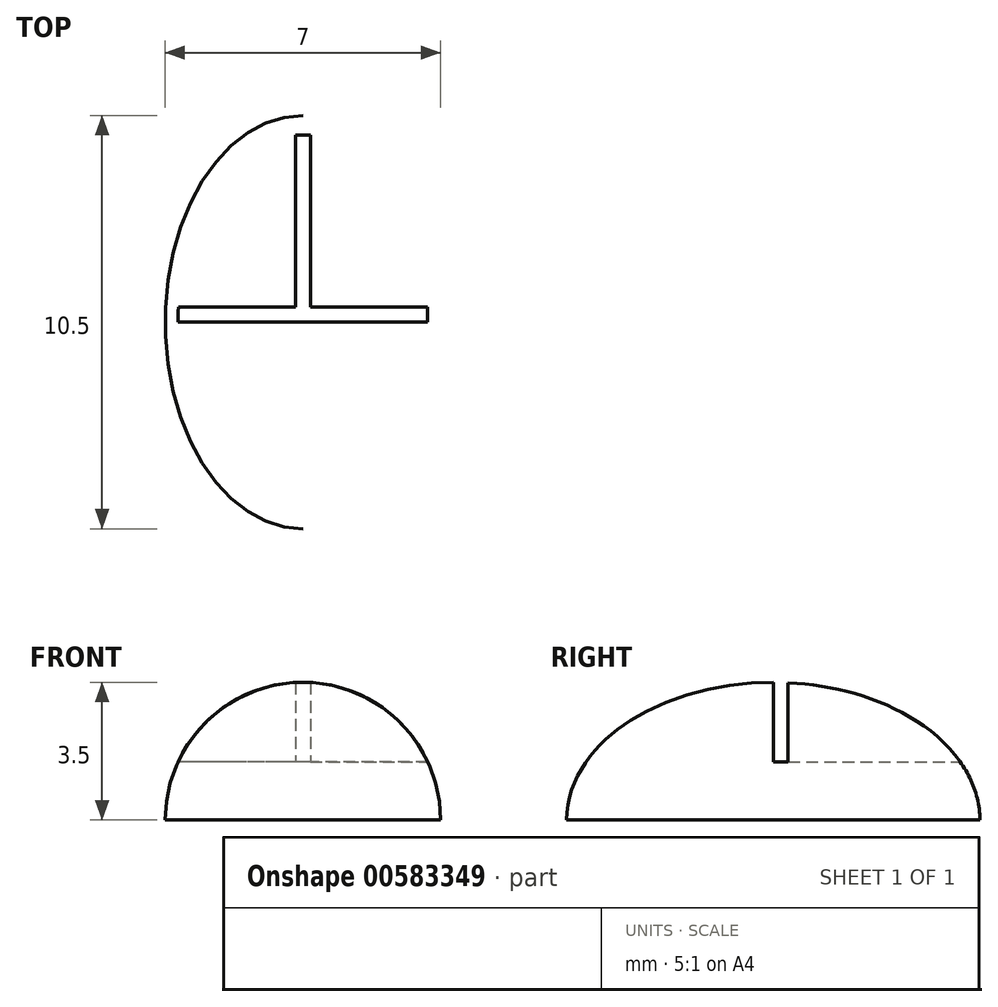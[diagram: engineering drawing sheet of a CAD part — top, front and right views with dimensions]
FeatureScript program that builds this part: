
annotation { "Feature Type Name" : "Feature", "Feature Type Description" : "" }
export const myFeature = defineFeature(function(context is Context, id is Id, definition is map)
    precondition{}
    {
        {
            var Q0;
            Q0=qCreatedBy(makeId("Top.planeOp"),FACE);
            var sketch = newSketch(context, id + "F0", { "sketchPlane" : qUnion([Q0])});
            skEllipticalArc(sketch, "E0", {});
            skLineSegment(sketch, "E1", {"start": v(0, 0) * mm, "end": v(0, 1.86) * mm});
            skPoint(sketch, "E1.endSnap0", {"position": v(0, 5.25) * mm});
            skLineSegment(sketch, "E2", {"start": v(0, 1.86) * mm, "end": v(0, 5.25) * mm});
            skLineSegment(sketch, "E3", {"start": v(0, 0) * mm, "end": v(0, -5.25) * mm});
            const initialGuessF0  = {"E0": [0, 0, 0, 1, 0.00525, 0.0035, 0, 3.141592653589793]};
            skSetInitialGuess(sketch, initialGuessF0);
            skSolve(sketch);
        }
        {
            var Q0;
            Q0 = qSketchRegion(id + "F0", true);
            var Q1;
            Q1=sQuery(id+"F0.wireOp",EDGE,"E2");
            revolve(context, id + "F1", {"entities" : qUnion([Q0]), "axis" : qUnion([Q1]), "revolveType" : RevolveType.FULL});
        }
        {
            var Q0;
            Q0=qCreatedBy(makeId("Right.planeOp"),FACE);
            var sketch = newSketch(context, id + "F2", { "sketchPlane" : qUnion([Q0])});
            skLineSegment(sketch, "E4", {"start": v(0, 0) * mm, "end": v(6.37, 0) * mm});
            skLineSegment(sketch, "E5", {"start": v(6.37, 0) * mm, "end": v(6.37, -3.6) * mm});
            skLineSegment(sketch, "E6", {"start": v(6.37, -3.6) * mm, "end": v(-6.3, -3.6) * mm});
            skLineSegment(sketch, "E7", {"start": v(-6.3, -3.6) * mm, "end": v(-6.3, 0) * mm});
            skLineSegment(sketch, "E8", {"start": v(-6.3, 0) * mm, "end": v(0, 0) * mm});
            skSolve(sketch);
        }
        {
            var Q0;
            Q0 = qSketchRegion(id + "F2", true);
            extrude(context, id + "F3", {"entities" : qUnion([Q0]), "operationType" : NewBodyOperationType.REMOVE, "oppositeDirection" : true, "depth" : 25 * mm, "offsetDistance" : 25 * mm, "hasSecondDirection" : true, "secondDirectionOppositeDirection" : false, "secondDirectionDepth" : 25 * mm});
        }
        {
            var Q0;
            Q0=qCreatedBy(makeId("Top.planeOp"),FACE);
            var sketch = newSketch(context, id + "F4", { "sketchPlane" : qUnion([Q0])});
            skLineSegment(sketch, "E9", {"start": v(0, 0) * mm, "end": v(4.51, 0) * mm});
            skLineSegment(sketch, "E10", {"start": v(0, 0) * mm, "end": v(-4.45, 0) * mm});
            skLineSegment(sketch, "E11.0", {"start": v(0.2, 0.38) * mm, "end": v(0.2, 5.2) * mm});
            skLineSegment(sketch, "E12.0", {"start": v(-0.2, 0.38) * mm, "end": v(-0.2, 5.2) * mm});
            skLineSegment(sketch, "E13", {"start": v(-0.2, 5.2) * mm, "end": v(-0.2, 5.45) * mm});
            skLineSegment(sketch, "E14", {"start": v(-0.2, 5.45) * mm, "end": v(0.2, 5.45) * mm});
            skLineSegment(sketch, "E15", {"start": v(0.2, 5.45) * mm, "end": v(0.2, 5.2) * mm});
            skLineSegment(sketch, "E16.0", {"start": v(-0.2, 0.38) * mm, "end": v(-4.45, 0.38) * mm});
            skLineSegment(sketch, "E17.0", {"start": v(0.2, 0.38) * mm, "end": v(4.51, 0.38) * mm});
            skLineSegment(sketch, "E18", {"start": v(-4.45, 0.38) * mm, "end": v(-4.45, 0) * mm});
            skLineSegment(sketch, "E19", {"start": v(4.51, 0.38) * mm, "end": v(4.51, 0) * mm});
            skSolve(sketch);
        }
        {
            var Q0;
            Q0 = qSketchRegion(id + "F4", true);
            extrude(context, id + "F5", {"entities" : qUnion([Q0]), "operationType" : NewBodyOperationType.REMOVE, "depth" : 11.5 * mm, "offsetDistance" : 25 * mm, "hasSecondDirection" : true, "secondDirectionOppositeDirection" : false, "secondDirectionDepth" : 1.48 * mm});
        }
    });
